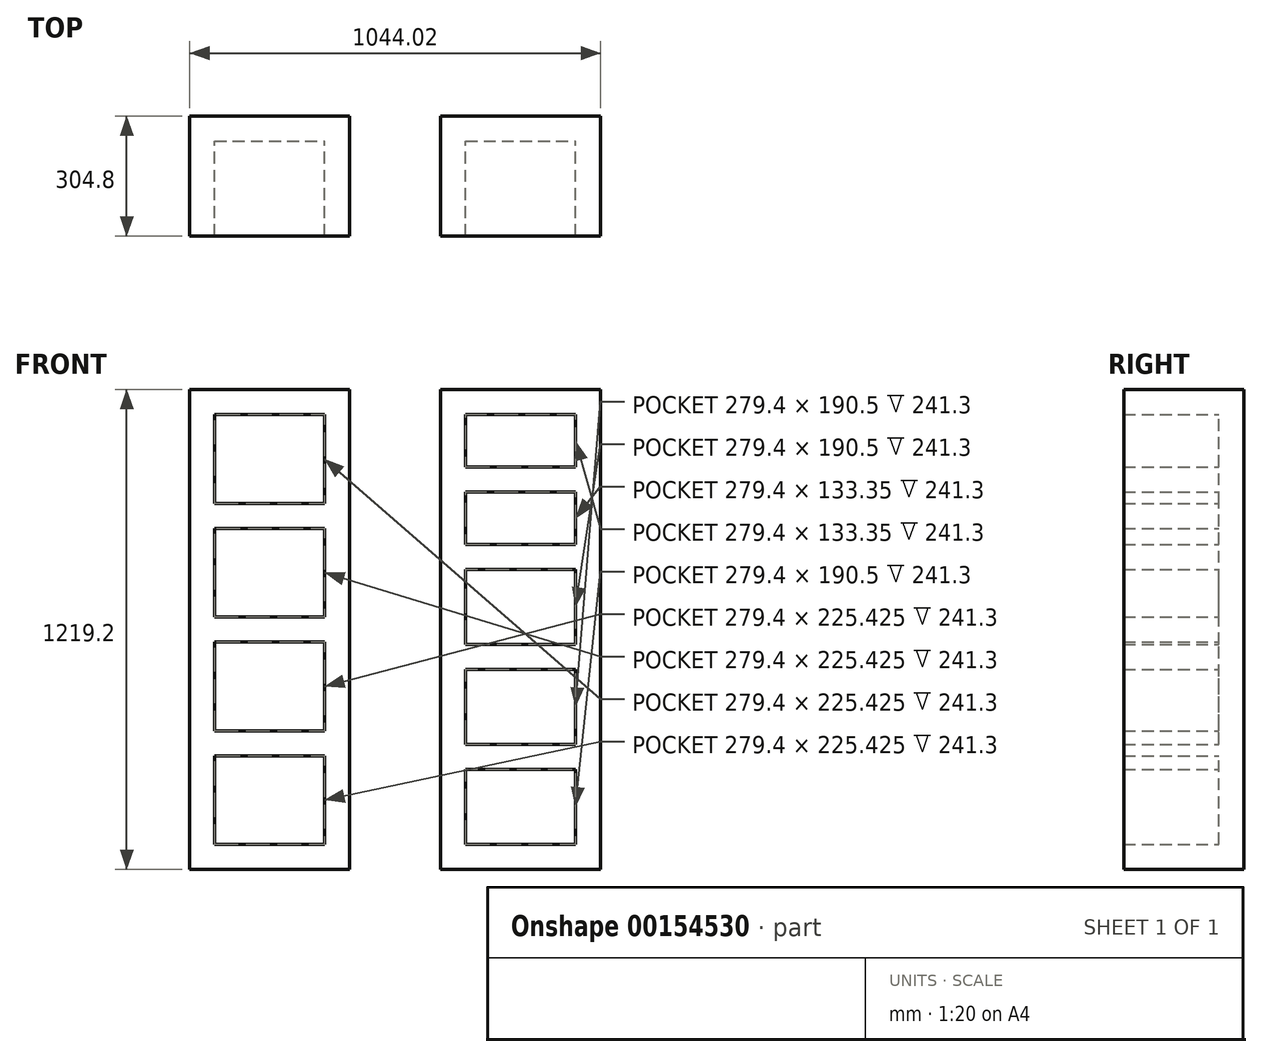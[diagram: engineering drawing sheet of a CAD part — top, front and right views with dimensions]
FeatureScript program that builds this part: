
annotation { "Feature Type Name" : "Feature", "Feature Type Description" : "" }
export const myFeature = defineFeature(function(context is Context, id is Id, definition is map)
    precondition{}
    {
        {
            var Q0;
            Q0=qCreatedBy(makeId("Front.planeOp"),FACE);
            var sketch = newSketch(context, id + "F0", { "sketchPlane" : qUnion([Q0])});
            skLineSegment(sketch, "E0.bottom", {"start": v(0, 0) * mm, "end": v(406.4, 0) * mm});
            skLineSegment(sketch, "E0.top", {"start": v(0, 1219.2) * mm, "end": v(406.4, 1219.2) * mm});
            skLineSegment(sketch, "E0.left", {"start": v(0, 0) * mm, "end": v(0, 1219.2) * mm});
            skLineSegment(sketch, "E0.right", {"start": v(406.4, 0) * mm, "end": v(406.4, 1219.2) * mm});
            skLineSegment(sketch, "E1.bottom", {"start": v(-231.22, 0) * mm, "end": v(-637.62, 0) * mm});
            skLineSegment(sketch, "E1.top", {"start": v(-231.22, 1219.2) * mm, "end": v(-637.62, 1219.2) * mm});
            skLineSegment(sketch, "E1.left", {"start": v(-231.22, 0) * mm, "end": v(-231.22, 1219.2) * mm});
            skLineSegment(sketch, "E1.right", {"start": v(-637.62, 0) * mm, "end": v(-637.62, 1219.2) * mm});
            skLineSegment(sketch, "E2.0", {"start": v(-294.72, 1155.7) * mm, "end": v(-574.12, 1155.7) * mm});
            skLineSegment(sketch, "E2.1", {"start": v(-294.72, 63.5) * mm, "end": v(-294.72, 1155.7) * mm});
            skLineSegment(sketch, "E2.2", {"start": v(-294.72, 63.5) * mm, "end": v(-574.12, 63.5) * mm});
            skLineSegment(sketch, "E2.3", {"start": v(-574.12, 63.5) * mm, "end": v(-574.12, 1155.7) * mm});
            skLineSegment(sketch, "E3.0", {"start": v(342.9, 63.5) * mm, "end": v(342.9, 1155.7) * mm});
            skLineSegment(sketch, "E3.1", {"start": v(63.5, 63.5) * mm, "end": v(342.9, 63.5) * mm});
            skLineSegment(sketch, "E3.2", {"start": v(63.5, 63.5) * mm, "end": v(63.5, 1155.7) * mm});
            skLineSegment(sketch, "E3.3", {"start": v(63.5, 1155.7) * mm, "end": v(342.9, 1155.7) * mm});
            skLineSegment(sketch, "E4.bottom", {"start": v(-574.12, 930.28) * mm, "end": v(-294.72, 930.28) * mm});
            skLineSegment(sketch, "E4.top", {"start": v(-574.12, 866.78) * mm, "end": v(-294.72, 866.78) * mm});
            skLineSegment(sketch, "E4.left", {"start": v(-574.12, 930.28) * mm, "end": v(-574.12, 866.78) * mm});
            skLineSegment(sketch, "E4.right", {"start": v(-294.72, 930.28) * mm, "end": v(-294.72, 866.78) * mm});
            skLineSegment(sketch, "E5.bottom", {"start": v(-574.12, 641.35) * mm, "end": v(-294.72, 641.35) * mm});
            skLineSegment(sketch, "E5.top", {"start": v(-574.12, 577.85) * mm, "end": v(-294.72, 577.85) * mm});
            skLineSegment(sketch, "E5.left", {"start": v(-574.12, 641.35) * mm, "end": v(-574.12, 577.85) * mm});
            skLineSegment(sketch, "E5.right", {"start": v(-294.72, 641.35) * mm, "end": v(-294.72, 577.85) * mm});
            skLineSegment(sketch, "E6.bottom", {"start": v(-574.12, 352.43) * mm, "end": v(-294.72, 352.43) * mm});
            skLineSegment(sketch, "E6.top", {"start": v(-574.12, 288.93) * mm, "end": v(-294.72, 288.93) * mm});
            skLineSegment(sketch, "E6.left", {"start": v(-574.12, 352.43) * mm, "end": v(-574.12, 288.93) * mm});
            skLineSegment(sketch, "E6.right", {"start": v(-294.72, 352.43) * mm, "end": v(-294.72, 288.93) * mm});
            skLineSegment(sketch, "E7", {"start": v(-434.42, 1155.7) * mm, "end": v(-434.42, 930.28) * mm, "construction": true});
            skLineSegment(sketch, "E8", {"start": v(-434.42, 930.28) * mm, "end": v(-434.42, 866.78) * mm, "construction": true});
            skLineSegment(sketch, "E9", {"start": v(-434.42, 866.78) * mm, "end": v(-434.42, 641.35) * mm, "construction": true});
            skLineSegment(sketch, "E10", {"start": v(-434.42, 641.35) * mm, "end": v(-434.42, 577.85) * mm, "construction": true});
            skLineSegment(sketch, "E11", {"start": v(-434.42, 577.85) * mm, "end": v(-434.42, 352.43) * mm, "construction": true});
            skLineSegment(sketch, "E12", {"start": v(-434.42, 352.43) * mm, "end": v(-434.42, 288.93) * mm, "construction": true});
            skLineSegment(sketch, "E13", {"start": v(-434.42, 288.93) * mm, "end": v(-434.42, 63.5) * mm, "construction": true});
            skLineSegment(sketch, "E14.bottom", {"start": v(63.5, 1022.35) * mm, "end": v(342.9, 1022.35) * mm});
            skLineSegment(sketch, "E14.top", {"start": v(63.5, 958.85) * mm, "end": v(342.9, 958.85) * mm});
            skLineSegment(sketch, "E14.left", {"start": v(63.5, 1022.35) * mm, "end": v(63.5, 958.85) * mm});
            skLineSegment(sketch, "E14.right", {"start": v(342.9, 1022.35) * mm, "end": v(342.9, 958.85) * mm});
            skLineSegment(sketch, "E15.bottom", {"start": v(63.5, 825.5) * mm, "end": v(342.9, 825.5) * mm});
            skLineSegment(sketch, "E15.top", {"start": v(63.5, 762) * mm, "end": v(342.9, 762) * mm});
            skLineSegment(sketch, "E15.left", {"start": v(63.5, 825.5) * mm, "end": v(63.5, 762) * mm});
            skLineSegment(sketch, "E15.right", {"start": v(342.9, 825.5) * mm, "end": v(342.9, 762) * mm});
            skLineSegment(sketch, "E16.bottom", {"start": v(63.5, 571.5) * mm, "end": v(342.9, 571.5) * mm});
            skLineSegment(sketch, "E16.top", {"start": v(63.5, 508) * mm, "end": v(342.9, 508) * mm});
            skLineSegment(sketch, "E16.left", {"start": v(63.5, 571.5) * mm, "end": v(63.5, 508) * mm});
            skLineSegment(sketch, "E16.right", {"start": v(342.9, 571.5) * mm, "end": v(342.9, 508) * mm});
            skLineSegment(sketch, "E17.bottom", {"start": v(63.5, 317.5) * mm, "end": v(342.9, 317.5) * mm});
            skLineSegment(sketch, "E17.top", {"start": v(63.5, 254) * mm, "end": v(342.9, 254) * mm});
            skLineSegment(sketch, "E17.left", {"start": v(63.5, 317.5) * mm, "end": v(63.5, 254) * mm});
            skLineSegment(sketch, "E17.right", {"start": v(342.9, 317.5) * mm, "end": v(342.9, 254) * mm});
            skLineSegment(sketch, "E18", {"start": v(203.2, 63.5) * mm, "end": v(203.2, 254) * mm, "construction": true});
            skLineSegment(sketch, "E19", {"start": v(203.2, 254) * mm, "end": v(203.2, 317.5) * mm, "construction": true});
            skLineSegment(sketch, "E20", {"start": v(203.2, 317.5) * mm, "end": v(203.2, 508) * mm, "construction": true});
            skLineSegment(sketch, "E21", {"start": v(203.2, 508) * mm, "end": v(203.2, 571.5) * mm, "construction": true});
            skLineSegment(sketch, "E22", {"start": v(203.2, 571.5) * mm, "end": v(203.2, 762) * mm, "construction": true});
            skLineSegment(sketch, "E23", {"start": v(203.2, 762) * mm, "end": v(203.2, 825.5) * mm, "construction": true});
            skLineSegment(sketch, "E24", {"start": v(203.2, 825.5) * mm, "end": v(203.2, 958.85) * mm, "construction": true});
            skLineSegment(sketch, "E25", {"start": v(203.2, 958.85) * mm, "end": v(203.2, 1022.35) * mm, "construction": true});
            skLineSegment(sketch, "E26", {"start": v(203.2, 1022.35) * mm, "end": v(203.2, 1155.7) * mm, "construction": true});
            skSolve(sketch);
        }
        {
            var Q0;
            Q0=makeQuery(id+"F0.imprint","IMPRINT",FACE,{"disambiguationData":[TD([[makeQuery(id+"F0.imprint","IMPRINT",EDGE,{"derivedFrom":sQuery(id+"F0.wireOp",EDGE,"E1.bottom")}),-1.0]])]});
            var Q1;
            Q1=makeQuery(id+"F0.imprint","IMPRINT",FACE,{"disambiguationData":[TD([[makeQuery(id+"F0.imprint","IMPRINT",EDGE,{"derivedFrom":sQuery(id+"F0.wireOp",EDGE,"E0.bottom")}),1.0]])]});
            var Q2;
            {var subQ0=sQuery(id+"F0.wireOp",EDGE,"E2.0");Q2=makeQuery(id+"F0.imprint","IMPRINT",FACE,{"disambiguationData":[TD([[makeQuery(id+"F0.imprint","IMPRINT",EDGE,{"derivedFrom":subQ0}),1.0]])]});}
            var Q3;
            Q3=makeQuery(id+"F0.imprint","IMPRINT",FACE,{"disambiguationData":[TD([[makeQuery(id+"F0.imprint","IMPRINT",EDGE,{"derivedFrom":sQuery(id+"F0.wireOp",EDGE,"E4.bottom")}),-1.0]])]});
            var Q4;
            {var subQ0=sQuery(id+"F0.wireOp",EDGE,"E4.top");Q4=makeQuery(id+"F0.imprint","IMPRINT",FACE,{"disambiguationData":[TD([[makeQuery(id+"F0.imprint","IMPRINT",EDGE,{"derivedFrom":subQ0}),-1.0]])]});}
            var Q5;
            Q5=makeQuery(id+"F0.imprint","IMPRINT",FACE,{"disambiguationData":[TD([[makeQuery(id+"F0.imprint","IMPRINT",EDGE,{"derivedFrom":sQuery(id+"F0.wireOp",EDGE,"E5.bottom")}),-1.0]])]});
            var Q6;
            {var subQ0=sQuery(id+"F0.wireOp",EDGE,"E5.top");Q6=makeQuery(id+"F0.imprint","IMPRINT",FACE,{"disambiguationData":[TD([[makeQuery(id+"F0.imprint","IMPRINT",EDGE,{"derivedFrom":subQ0}),-1.0]])]});}
            var Q7;
            Q7=makeQuery(id+"F0.imprint","IMPRINT",FACE,{"disambiguationData":[TD([[makeQuery(id+"F0.imprint","IMPRINT",EDGE,{"derivedFrom":sQuery(id+"F0.wireOp",EDGE,"E6.bottom")}),-1.0]])]});
            var Q8;
            {var subQ0=sQuery(id+"F0.wireOp",EDGE,"E2.2");Q8=makeQuery(id+"F0.imprint","IMPRINT",FACE,{"disambiguationData":[TD([[makeQuery(id+"F0.imprint","IMPRINT",EDGE,{"derivedFrom":subQ0}),-1.0]])]});}
            var Q9;
            {var subQ0=sQuery(id+"F0.wireOp",EDGE,"E3.1");Q9=makeQuery(id+"F0.imprint","IMPRINT",FACE,{"disambiguationData":[TD([[makeQuery(id+"F0.imprint","IMPRINT",EDGE,{"derivedFrom":subQ0}),1.0]])]});}
            var Q10;
            Q10=makeQuery(id+"F0.imprint","IMPRINT",FACE,{"disambiguationData":[TD([[makeQuery(id+"F0.imprint","IMPRINT",EDGE,{"derivedFrom":sQuery(id+"F0.wireOp",EDGE,"E17.bottom")}),-1.0]])]});
            var Q11;
            {var subQ0=sQuery(id+"F0.wireOp",EDGE,"E16.top");Q11=makeQuery(id+"F0.imprint","IMPRINT",FACE,{"disambiguationData":[TD([[makeQuery(id+"F0.imprint","IMPRINT",EDGE,{"derivedFrom":subQ0}),-1.0]])]});}
            var Q12;
            Q12=makeQuery(id+"F0.imprint","IMPRINT",FACE,{"disambiguationData":[TD([[makeQuery(id+"F0.imprint","IMPRINT",EDGE,{"derivedFrom":sQuery(id+"F0.wireOp",EDGE,"E16.bottom")}),-1.0]])]});
            var Q13;
            {var subQ0=sQuery(id+"F0.wireOp",EDGE,"E15.top");Q13=makeQuery(id+"F0.imprint","IMPRINT",FACE,{"disambiguationData":[TD([[makeQuery(id+"F0.imprint","IMPRINT",EDGE,{"derivedFrom":subQ0}),-1.0]])]});}
            var Q14;
            Q14=makeQuery(id+"F0.imprint","IMPRINT",FACE,{"disambiguationData":[TD([[makeQuery(id+"F0.imprint","IMPRINT",EDGE,{"derivedFrom":sQuery(id+"F0.wireOp",EDGE,"E15.bottom")}),-1.0]])]});
            var Q15;
            {var subQ0=sQuery(id+"F0.wireOp",EDGE,"E14.top");Q15=makeQuery(id+"F0.imprint","IMPRINT",FACE,{"disambiguationData":[TD([[makeQuery(id+"F0.imprint","IMPRINT",EDGE,{"derivedFrom":subQ0}),-1.0]])]});}
            var Q16;
            Q16=makeQuery(id+"F0.imprint","IMPRINT",FACE,{"disambiguationData":[TD([[makeQuery(id+"F0.imprint","IMPRINT",EDGE,{"derivedFrom":sQuery(id+"F0.wireOp",EDGE,"E14.bottom")}),-1.0]])]});
            var Q17;
            {var subQ0=sQuery(id+"F0.wireOp",EDGE,"E3.3");Q17=makeQuery(id+"F0.imprint","IMPRINT",FACE,{"disambiguationData":[TD([[makeQuery(id+"F0.imprint","IMPRINT",EDGE,{"derivedFrom":subQ0}),-1.0]])]});}
            extrude(context, id + "F1", {"entities" : qUnion([Q0, Q1, Q2, Q3, Q4, Q5, Q6, Q7, Q8, Q9, Q10, Q11, Q12, Q13, Q14, Q15, Q16, Q17]), "oppositeDirection" : true, "depth" : 63.5 * mm});
        }
        {
            var Q0;
            Q0=makeQuery(id+"F0.imprint","IMPRINT",FACE,{"disambiguationData":[TD([[makeQuery(id+"F0.imprint","IMPRINT",EDGE,{"derivedFrom":sQuery(id+"F0.wireOp",EDGE,"E1.bottom")}),-1.0]])]});
            var Q1;
            Q1=makeQuery(id+"F0.imprint","IMPRINT",FACE,{"disambiguationData":[TD([[makeQuery(id+"F0.imprint","IMPRINT",EDGE,{"derivedFrom":sQuery(id+"F0.wireOp",EDGE,"E4.bottom")}),-1.0]])]});
            var Q2;
            Q2=makeQuery(id+"F0.imprint","IMPRINT",FACE,{"disambiguationData":[TD([[makeQuery(id+"F0.imprint","IMPRINT",EDGE,{"derivedFrom":sQuery(id+"F0.wireOp",EDGE,"E5.bottom")}),-1.0]])]});
            var Q3;
            Q3=makeQuery(id+"F0.imprint","IMPRINT",FACE,{"disambiguationData":[TD([[makeQuery(id+"F0.imprint","IMPRINT",EDGE,{"derivedFrom":sQuery(id+"F0.wireOp",EDGE,"E6.bottom")}),-1.0]])]});
            var Q4;
            Q4=makeQuery(id+"F0.imprint","IMPRINT",FACE,{"disambiguationData":[TD([[makeQuery(id+"F0.imprint","IMPRINT",EDGE,{"derivedFrom":sQuery(id+"F0.wireOp",EDGE,"E0.bottom")}),1.0]])]});
            var Q5;
            Q5=makeQuery(id+"F0.imprint","IMPRINT",FACE,{"disambiguationData":[TD([[makeQuery(id+"F0.imprint","IMPRINT",EDGE,{"derivedFrom":sQuery(id+"F0.wireOp",EDGE,"E14.bottom")}),-1.0]])]});
            var Q6;
            Q6=makeQuery(id+"F0.imprint","IMPRINT",FACE,{"disambiguationData":[TD([[makeQuery(id+"F0.imprint","IMPRINT",EDGE,{"derivedFrom":sQuery(id+"F0.wireOp",EDGE,"E15.bottom")}),-1.0]])]});
            var Q7;
            Q7=makeQuery(id+"F0.imprint","IMPRINT",FACE,{"disambiguationData":[TD([[makeQuery(id+"F0.imprint","IMPRINT",EDGE,{"derivedFrom":sQuery(id+"F0.wireOp",EDGE,"E16.bottom")}),-1.0]])]});
            var Q8;
            Q8=makeQuery(id+"F0.imprint","IMPRINT",FACE,{"disambiguationData":[TD([[makeQuery(id+"F0.imprint","IMPRINT",EDGE,{"derivedFrom":sQuery(id+"F0.wireOp",EDGE,"E17.bottom")}),-1.0]])]});
            extrude(context, id + "F2", {"entities" : qUnion([Q0, Q1, Q2, Q3, Q4, Q5, Q6, Q7, Q8]), "operationType" : NewBodyOperationType.ADD, "depth" : 241.3 * mm});
        }
    });
